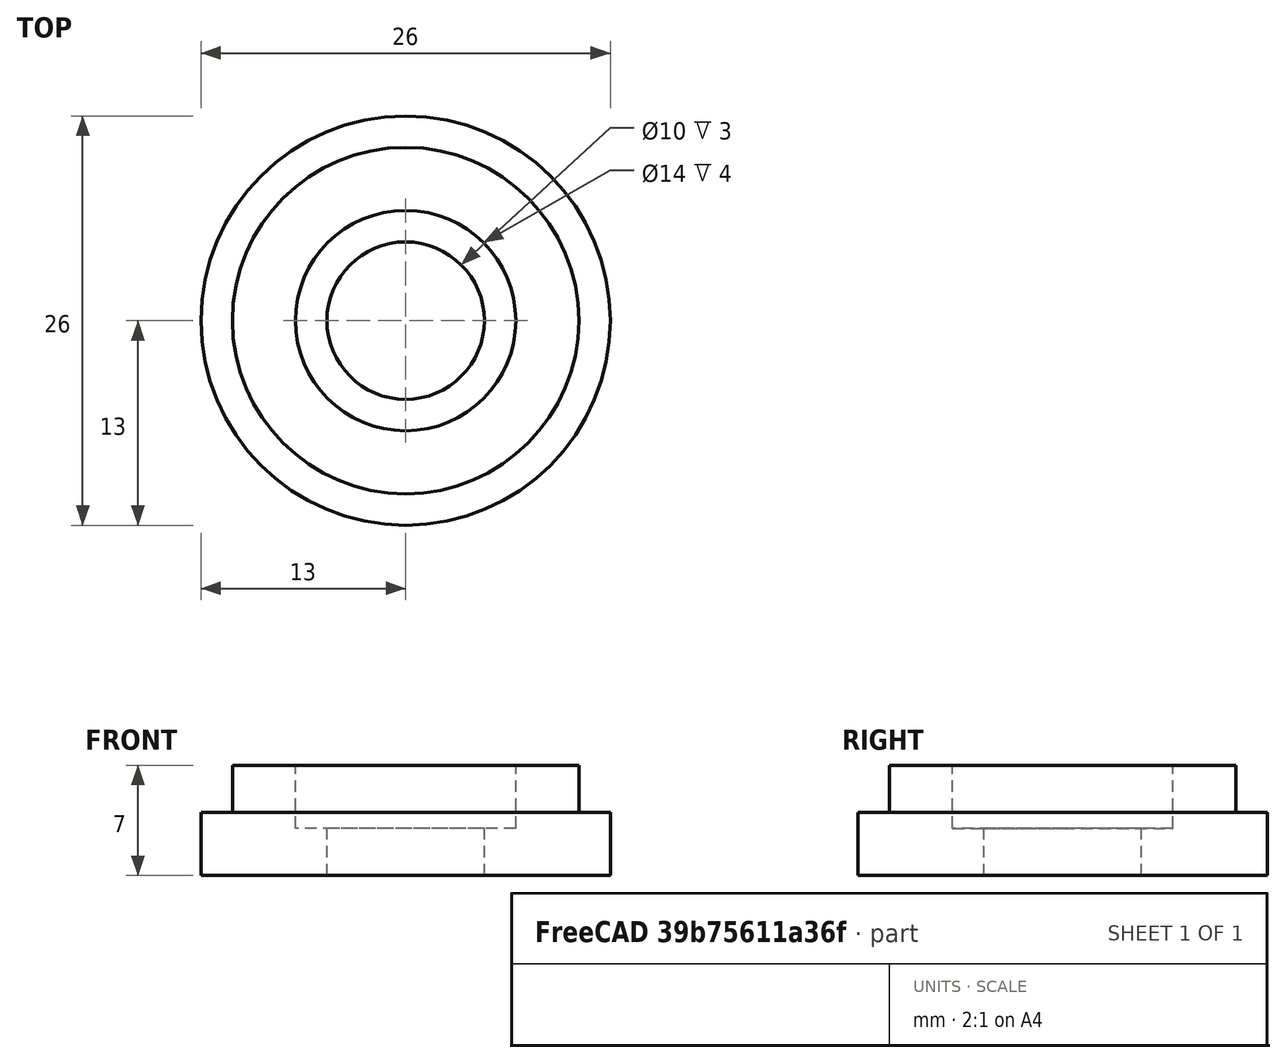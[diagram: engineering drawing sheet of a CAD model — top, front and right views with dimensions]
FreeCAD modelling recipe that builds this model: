
FCSTD DOCUMENT  (FreeCAD 0.19R24276 (Git))
Label: espaciador plano
License: All rights reserved
LicenseURL: http://en.wikipedia.org/wiki/All_rights_reserved
objects: TechDraw::DrawViewDimension×9, Part::Cylinder×4, TechDraw::DrawProjGroupItem×3, Part::Cut×2, TechDraw::DrawSVGTemplate×2, TechDraw::DrawViewPart×2, TechDraw::DrawPage×2, Part::Fuse×1, TechDraw::DrawProjGroup×1, TechDraw::DrawViewAnnotation×1
note: 7 computed .brp shape members not serialized (recipe doc carries the construction recipe); baked Part::Feature solids carry a one-line shape summary decoded from their .brp

FEATURE [Part::Cylinder] Cylinder  label="Cilindro"
  Angle = 360
  AttacherType = Attacher::AttachEngine3D
  Height = 4
  Radius = 13
FEATURE [Part::Cylinder] Cylinder001  label="Cilindro001"
  Angle = 360
  AttacherType = Attacher::AttachEngine3D
  Height = 3
  Placement = pos=(0,0,4) rot=(0,0,1;0rad)
  Radius = 11
FEATURE [Part::Cylinder] Cylinder002  label="Cilindro002"
  Angle = 360
  AttacherType = Attacher::AttachEngine3D
  Height = 7
  Radius = 5
FEATURE [Part::Fuse] Fusion
  Base = -> Cylinder
  Tool = -> Cylinder001
FEATURE [Part::Cut] Cut
  Base = -> Fusion
  Tool = -> Cylinder002
FEATURE [Part::Cylinder] Cylinder003  label="Cilindro003"
  Angle = 360
  AttacherType = Attacher::AttachEngine3D
  Height = 4
  Placement = pos=(0,0,3) rot=(0,0,1;0rad)
  Radius = 7
FEATURE [Part::Cut] Cut001
  Base = -> Cut
  Tool = -> Cylinder003
FEATURE [TechDraw::DrawSVGTemplate] Template
  EditableTexts = Designed_by_Name=<owner>; Drawing_number=001; FC-Date=-; FC-SC=1:1; FC-SH=5/10; FC-Title=Flat Spacer; Subtitle=Espaciador Plano; Weight=<100gr
  Height = 210
  Orientation = 1
  Width = 297
FEATURE [TechDraw::DrawSVGTemplate] Template001
  EditableTexts = Designed_by_Name=<owner>; Drawing_number=001; FC-Date=-; FC-SC=4:1; FC-SH=6/10; FC-Title=Flat Spacer; Subtitle=Espaciador Plano; Weight=<100gr
  Height = 210
  Orientation = 1
  Width = 297
FEATURE [TechDraw::DrawViewPart] View
  CoarseView = false
  Direction = (0.577,-0.577,0.577)
  Focus = 100
  HardHidden = false
  IsoCount = 0
  IsoHidden = false
  IsoVisible = false
  LockPosition = false
  Perspective = false
  Rotation = 0
  Scale = 4
  ScaleType = 0
  SeamHidden = false
  SeamVisible = true
  SmoothHidden = false
  SmoothVisible = true
  Source = -> [Cut001]
  X = 203.825
  XDirection = (0.707,0.707,0)
  Y = 134.61
FEATURE [TechDraw::DrawViewPart] View001
  CoarseView = false
  Direction = (0.577,-0.577,0.577)
  Focus = 100
  HardHidden = false
  IsoCount = 0
  IsoHidden = false
  IsoVisible = false
  LockPosition = false
  Perspective = false
  Rotation = 0
  Scale = 4
  ScaleType = 0
  SeamHidden = false
  SeamVisible = true
  SmoothHidden = false
  SmoothVisible = true
  Source = -> [Cut001]
  X = 154.141
  XDirection = (0.707,0.707,0)
  Y = 133.508
FEATURE [TechDraw::DrawProjGroupItem] ProjItem  label="Front"
  CoarseView = false
  Direction = (0,-1,0)
  Focus = 100
  HardHidden = false
  IsoCount = 0
  IsoHidden = false
  IsoVisible = false
  LockPosition = true
  Perspective = false
  Rotation = 0
  RotationVector = (1,0,0)
  ScaleType = 2
  SeamHidden = false
  SeamVisible = true
  SmoothHidden = false
  SmoothVisible = true
  Source = -> [Cut001]
  Type = 0
  X = 0
  XDirection = (1,0,0)
  Y = 0
FEATURE [TechDraw::DrawProjGroupItem] ProjItem001  label="Top"
  CoarseView = false
  Direction = (0,0,1)
  Focus = 100
  HardHidden = false
  IsoCount = 0
  IsoHidden = false
  IsoVisible = false
  LockPosition = false
  Perspective = false
  Rotation = 0
  RotationVector = (1,0,0)
  ScaleType = 2
  SeamHidden = false
  SeamVisible = true
  SmoothHidden = false
  SmoothVisible = true
  Source = -> [Cut001]
  Type = 4
  X = 0
  XDirection = (1,0,0)
  Y = -41
FEATURE [TechDraw::DrawProjGroupItem] ProjItem002  label="Bottom"
  CoarseView = false
  Direction = (0,0,-1)
  Focus = 100
  HardHidden = false
  IsoCount = 0
  IsoHidden = false
  IsoVisible = false
  LockPosition = false
  Perspective = false
  Rotation = 0
  RotationVector = (1,0,0)
  ScaleType = 2
  SeamHidden = false
  SeamVisible = true
  SmoothHidden = false
  SmoothVisible = true
  Source = -> [Cut001]
  Type = 5
  X = 0
  XDirection = (1,0,0)
  Y = 41
FEATURE [TechDraw::DrawProjGroup] ProjGroup
  Anchor = -> ProjItem
  AutoDistribute = true
  LockPosition = false
  ProjectionType = 0
  Rotation = 0
  ScaleType = 2
  Source = -> [Cut001]
  Views = -> [ProjItem,ProjItem001,ProjItem002]
  X = 90.0584
  Y = 116.299
  spacingX = 15
  spacingY = 15
FEATURE [TechDraw::DrawViewDimension] Dimension
  Arbitrary = false
  ArbitraryTolerances = false
  EqualTolerance = true
  FormatSpec = %.2f
  FormatSpecOverTolerance = %+.2f
  FormatSpecUnderTolerance = %+.2f
  Inverted = false
  LockPosition = false
  MeasureType = 1
  OverTolerance = 0
  References2D = -> [ProjItem]
  Rotation = 0
  ScaleType = 0
  TheoreticalExact = false
  Type = 1
  UnderTolerance = 0
  X = -2.70563
  Y = -5.30375
FEATURE [TechDraw::DrawViewDimension] Dimension001
  Arbitrary = false
  ArbitraryTolerances = false
  EqualTolerance = true
  FormatSpec = %.2f
  FormatSpecOverTolerance = %+.2f
  FormatSpecUnderTolerance = %+.2f
  Inverted = false
  LockPosition = false
  MeasureType = 1
  OverTolerance = 0
  References2D = -> [ProjItem]
  Rotation = 0
  ScaleType = 0
  TheoreticalExact = false
  Type = 2
  UnderTolerance = 0
  X = -32.7431
  Y = -4.05844
FEATURE [TechDraw::DrawViewDimension] Dimension002
  Arbitrary = false
  ArbitraryTolerances = false
  EqualTolerance = true
  FormatSpec = ⌀%.2f
  FormatSpecOverTolerance = %+.2f
  FormatSpecUnderTolerance = %+.2f
  Inverted = false
  LockPosition = false
  MeasureType = 1
  OverTolerance = 0
  References2D = -> [ProjItem001]
  Rotation = 0
  ScaleType = 0
  TheoreticalExact = false
  Type = 5
  UnderTolerance = 0
  X = 20.9686
  Y = 21.645
FEATURE [TechDraw::DrawViewDimension] Dimension003
  Arbitrary = false
  ArbitraryTolerances = false
  EqualTolerance = true
  FormatSpec = ⌀%.2f
  FormatSpecOverTolerance = %+.2f
  FormatSpecUnderTolerance = %+.2f
  Inverted = false
  LockPosition = false
  MeasureType = 1
  OverTolerance = 0
  References2D = -> [ProjItem002]
  Rotation = 0
  ScaleType = 0
  TheoreticalExact = false
  Type = 5
  UnderTolerance = 0
  X = 25.5716
  Y = 23.2517
FEATURE [TechDraw::DrawPage] Page  label="Vistas"
  KeepUpdated = true
  NextBalloonIndex = 1
  ProjectionType = 0
  Template = -> Template
  Views = -> [View,ProjGroup,Dimension,Dimension001,Dimension002,Dimension003]
FEATURE [TechDraw::DrawViewDimension] Dimension004
  Arbitrary = false
  ArbitraryTolerances = false
  EqualTolerance = true
  FormatSpec = %.2f
  FormatSpecOverTolerance = %+.2f
  FormatSpecUnderTolerance = %+.2f
  Inverted = false
  LockPosition = false
  MeasureType = 1
  OverTolerance = 0
  References2D = -> [View001]
  Rotation = 0
  ScaleType = 0
  TheoreticalExact = false
  Type = 2
  UnderTolerance = 0
  X = 61.9319
  Y = -28.9592
FEATURE [TechDraw::DrawViewDimension] Dimension005
  Arbitrary = false
  ArbitraryTolerances = false
  EqualTolerance = true
  FormatSpec = %.2f
  FormatSpecOverTolerance = %+.2f
  FormatSpecUnderTolerance = %+.2f
  Inverted = false
  LockPosition = false
  MeasureType = 1
  OverTolerance = 0
  References2D = -> [View001]
  Rotation = 0
  ScaleType = 0
  TheoreticalExact = false
  Type = 2
  UnderTolerance = 0
  X = 54.6517
  Y = 9.54728
FEATURE [TechDraw::DrawViewDimension] Dimension006
  Arbitrary = false
  ArbitraryTolerances = false
  EqualTolerance = true
  FormatSpec = ⌀%.2f
  FormatSpecOverTolerance = %+.2f
  FormatSpecUnderTolerance = %+.2f
  Inverted = false
  LockPosition = false
  MeasureType = 1
  OverTolerance = 0
  References2D = -> [View001]
  Rotation = 0
  ScaleType = 0
  TheoreticalExact = false
  Type = 5
  UnderTolerance = 0
  X = 2.1645
  Y = 21.1039
FEATURE [TechDraw::DrawViewDimension] Dimension007
  Arbitrary = false
  ArbitraryTolerances = false
  EqualTolerance = true
  FormatSpec = %.2f
  FormatSpecOverTolerance = %+.2f
  FormatSpecUnderTolerance = %+.2f
  Inverted = false
  LockPosition = false
  MeasureType = 1
  OverTolerance = 0
  References2D = -> [View001]
  Rotation = 0
  ScaleType = 0
  TheoreticalExact = false
  Type = 1
  UnderTolerance = 0
  X = -82.3615
  Y = 3.40127
FEATURE [TechDraw::DrawViewDimension] Dimension008
  Arbitrary = false
  ArbitraryTolerances = false
  EqualTolerance = true
  FormatSpec = %.2f
  FormatSpecOverTolerance = %+.2f
  FormatSpecUnderTolerance = %+.2f
  Inverted = false
  LockPosition = false
  MeasureType = 1
  OverTolerance = 0
  References2D = -> [View001]
  Rotation = 0
  ScaleType = 0
  TheoreticalExact = false
  Type = 1
  UnderTolerance = 0
  X = -78.7489
  Y = 22.6689
FEATURE [TechDraw::DrawViewAnnotation] Annotation
  Font = osifont
  LineSpace = 80
  LockPosition = false
  MaxWidth = -1
  Rotation = 0
  ScaleType = 0
  Text = Aproximate measurements: | Check with 3D piece
  TextSize = 5
  TextStyle = 0
  X = 70.1
  Y = 65.4
FEATURE [TechDraw::DrawPage] Page001  label="Cotas"
  KeepUpdated = true
  NextBalloonIndex = 1
  ProjectionType = 0
  Template = -> Template001
  Views = -> [View001,Dimension004,Dimension005,Dimension006,Dimension007,Dimension008,Annotation]
